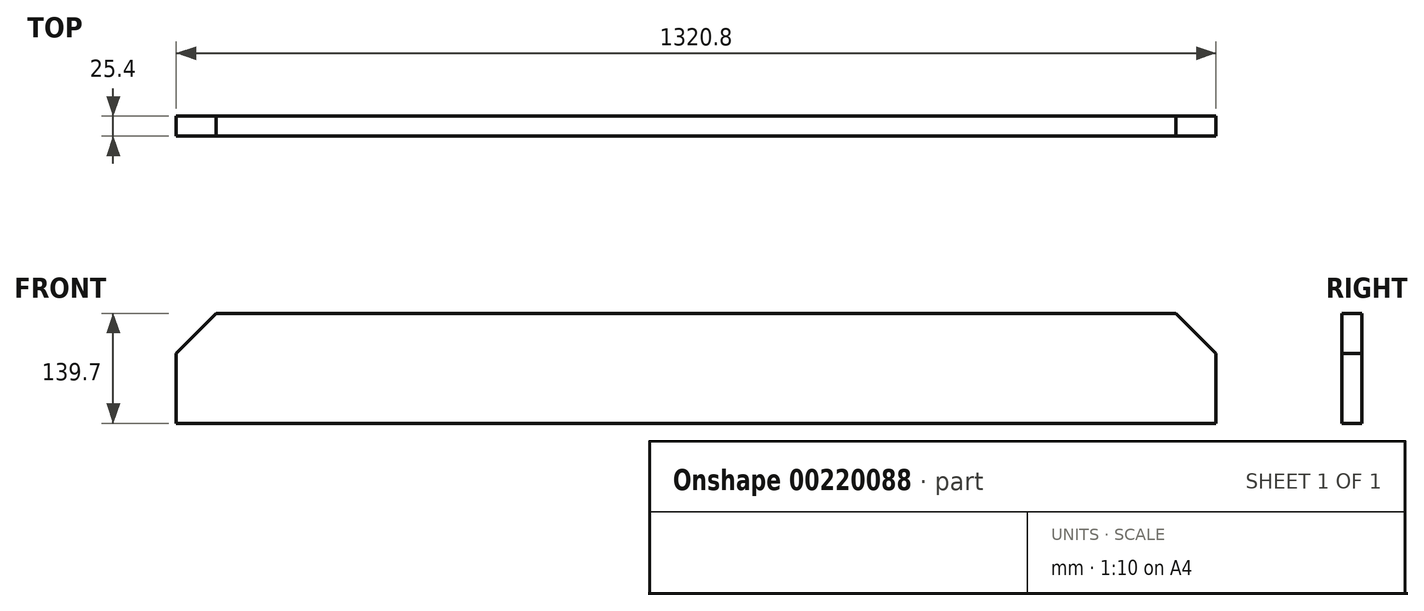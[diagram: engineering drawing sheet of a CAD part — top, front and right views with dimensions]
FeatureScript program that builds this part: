
annotation { "Feature Type Name" : "Feature", "Feature Type Description" : "" }
export const myFeature = defineFeature(function(context is Context, id is Id, definition is map)
    precondition{}
    {
        {
            var Q0;
            Q0=qCreatedBy(makeId("Right.planeOp"),FACE);
            var sketch = newSketch(context, id + "F0", { "sketchPlane" : qUnion([Q0])});
            skLineSegment(sketch, "E0.bottom", {"start": v(12.7, 69.85) * mm, "end": v(-12.7, 69.85) * mm});
            skLineSegment(sketch, "E0.top", {"start": v(12.7, -69.85) * mm, "end": v(-12.7, -69.85) * mm});
            skLineSegment(sketch, "E0.left", {"start": v(12.7, 69.85) * mm, "end": v(12.7, -69.85) * mm});
            skLineSegment(sketch, "E0.right", {"start": v(-12.7, 69.85) * mm, "end": v(-12.7, -69.85) * mm});
            skPoint(sketch, "E0.middle", {"position": v(0, 0) * mm});
            skSolve(sketch);
        }
        {
            var Q0;
            Q0 = qSketchRegion(id + "F0", true);
            extrude(context, id + "F1", {"entities" : qUnion([Q0]), "endBound" : BoundingType.SYMMETRIC, "depth" : 1320.8 * mm});
        }
        {
            var Q0;
            Q0=makeQuery(id+"F1.opExtrude","CAP_EDGE",EDGE,{"disambiguationData":[OSD([sQuery(id+"F0.wireOp",EDGE,"E0.bottom")])],"isStart":false});
            var Q1;
            Q1=makeQuery(id+"F1.opExtrude","CAP_EDGE",EDGE,{"disambiguationData":[OSD([sQuery(id+"F0.wireOp",EDGE,"E0.bottom")])],"isStart":true});
            chamfer(context, id + "F2", {"entities" : qUnion([Q0, Q1]), "width" : 50.8 * mm, "tangentPropagation" : true});
        }
    });
